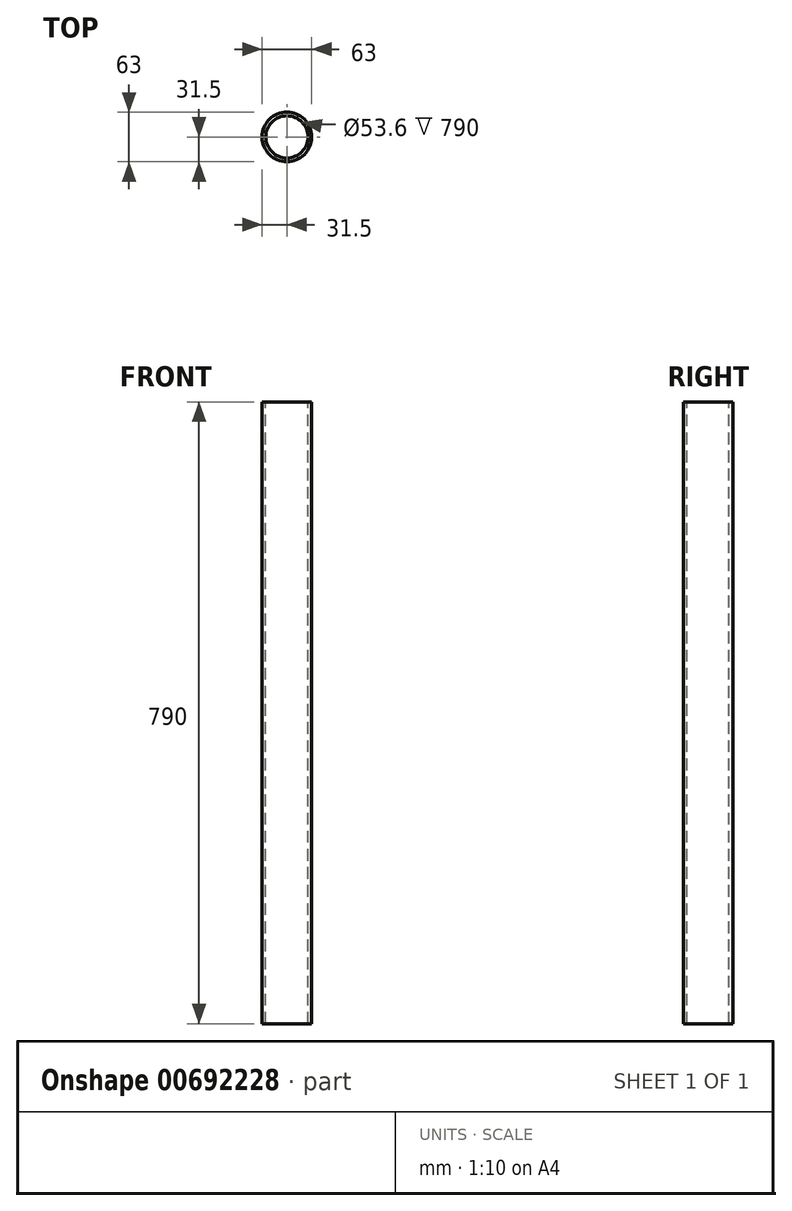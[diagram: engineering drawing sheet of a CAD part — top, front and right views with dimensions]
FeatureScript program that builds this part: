
annotation { "Feature Type Name" : "Feature", "Feature Type Description" : "" }
export const myFeature = defineFeature(function(context is Context, id is Id, definition is map)
    precondition{}
    {
        {
            var Q0;
            Q0=qCreatedBy(makeId("Front.planeOp"),FACE);
            var sketch = newSketch(context, id + "F0", { "sketchPlane" : qUnion([Q0])});
            skLineSegment(sketch, "E0", {"start": v(-31.5, 0) * mm, "end": v(-31.5, 790) * mm});
            skLineSegment(sketch, "E1", {"start": v(-31.5, 790) * mm, "end": v(-26.8, 790) * mm});
            skLineSegment(sketch, "E2", {"start": v(-26.8, 790) * mm, "end": v(-26.8, 0) * mm});
            skLineSegment(sketch, "E3", {"start": v(-26.8, 0) * mm, "end": v(-31.5, 0) * mm});
            skLineSegment(sketch, "E4", {"start": v(0, 0) * mm, "end": v(0, -19.02) * mm});
            skSolve(sketch);
        }
        {
            var Q0;
            Q0 = qSketchRegion(id + "F0", true);
            var Q1;
            Q1=sQuery(id+"F0.wireOp",EDGE,"E4");
            revolve(context, id + "F1", {"entities" : qUnion([Q0]), "axis" : qUnion([Q1]), "revolveType" : RevolveType.FULL});
        }
    });
